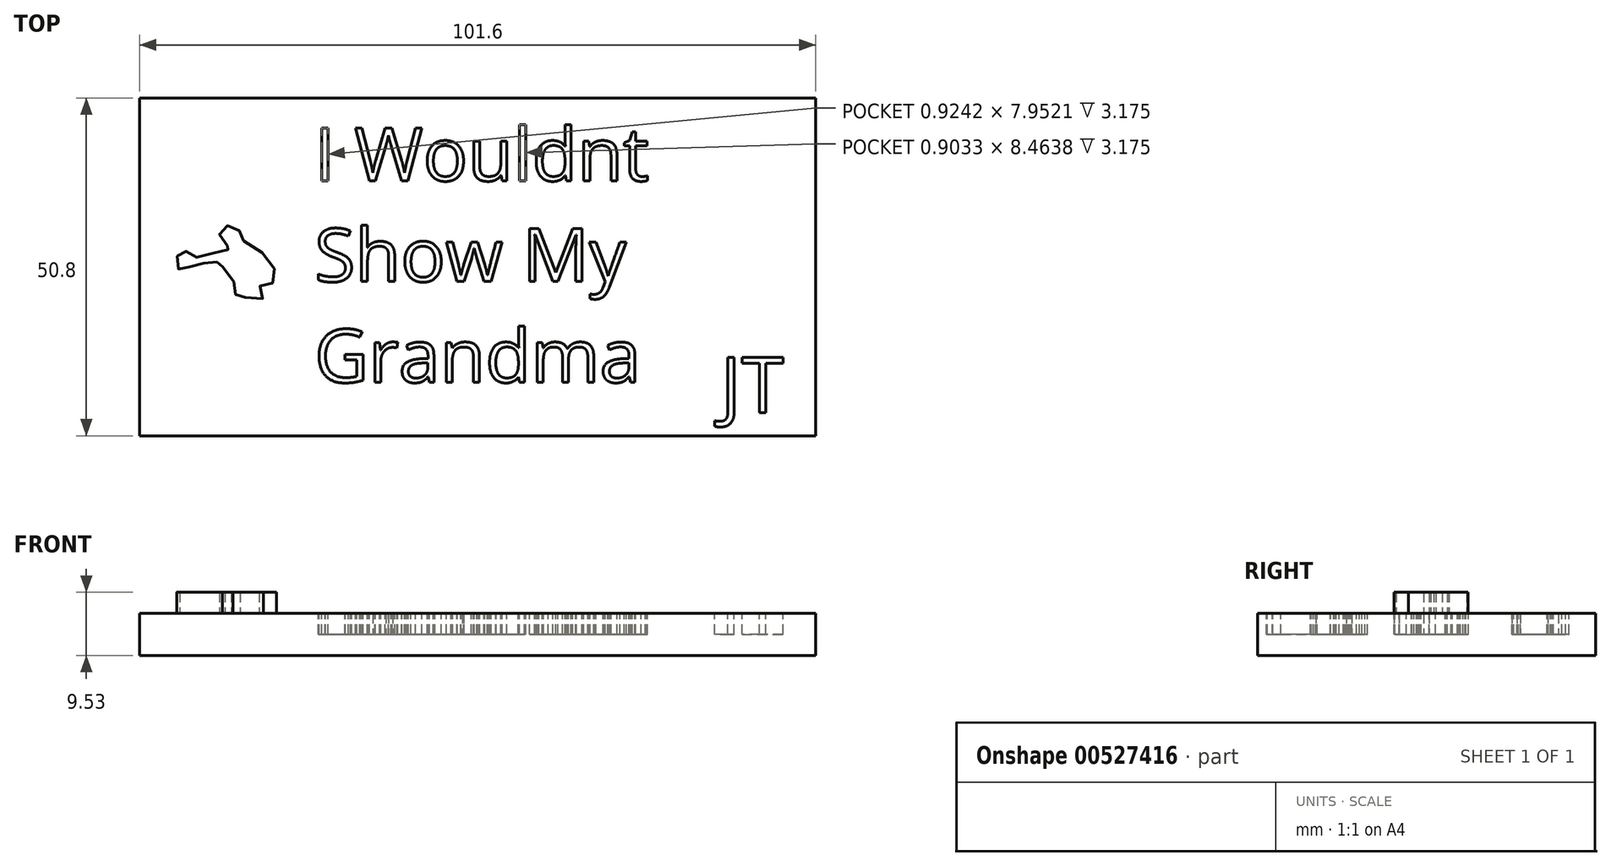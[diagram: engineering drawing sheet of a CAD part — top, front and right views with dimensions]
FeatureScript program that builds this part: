
annotation { "Feature Type Name" : "Feature", "Feature Type Description" : "" }
export const myFeature = defineFeature(function(context is Context, id is Id, definition is map)
    precondition{}
    {
        {
            var Q0;
            Q0=qCreatedBy(makeId("Top.planeOp"),FACE);
            var sketch = newSketch(context, id + "F0", { "sketchPlane" : qUnion([Q0])});
            skLineSegment(sketch, "E0.bottom", {"start": v(-49.76, 12.5) * mm, "end": v(51.84, 12.5) * mm});
            skLineSegment(sketch, "E0.top", {"start": v(-49.76, -38.3) * mm, "end": v(51.84, -38.3) * mm});
            skLineSegment(sketch, "E0.left", {"start": v(-49.76, 12.5) * mm, "end": v(-49.76, -38.3) * mm});
            skLineSegment(sketch, "E0.right", {"start": v(51.84, 12.5) * mm, "end": v(51.84, -38.3) * mm});
            skSolve(sketch);
        }
        {
            var Q0;
            Q0=makeQuery(id+"F0.imprint","IMPRINT",FACE,{"disambiguationData":[TD([[makeQuery(id+"F0.imprint","IMPRINT",EDGE,{"derivedFrom":sQuery(id+"F0.wireOp",EDGE,"E0.bottom")}),-1.0]])]});
            extrude(context, id + "F1", {"entities" : qUnion([Q0]), "depth" : 6.35 * mm, "offsetDistance" : 25.4 * mm});
        }
        {
            var Q0;
            Q0=makeQuery(id+"F1.opExtrude","CAP_FACE",FACE,{"disambiguationData":[OSD([sQuery(id+"F0.wireOp",EDGE,"E0.bottom"),sQuery(id+"F0.wireOp",EDGE,"E0.top"),sQuery(id+"F0.wireOp",EDGE,"E0.left"),sQuery(id+"F0.wireOp",EDGE,"E0.right")])],"isStart":false});
            var sketch = newSketch(context, id + "F2", { "sketchPlane" : qUnion([Q0])});
            skText(sketch, "E1", { "text": "I Wouldnt\nShow My\nGrandma", "fontName": "OpenSans-Regular.ttf"});
            const initialGuessF2  = {"E1": [-0.02347, 6e-05, 1, 0, 0.00802]};
            skSetInitialGuess(sketch, initialGuessF2);
            skSolve(sketch);
        }
        {
            var Q0;
            Q0=makeQuery(id+"F2.imprint","IMPRINT",FACE,{"disambiguationData":[TD([[makeQuery(id+"F2.imprint","IMPRINT",EDGE,{"derivedFrom":sQuery(id+"F2.wireOp",EDGE,"E1.sketch_text.stroke-0")}),-1.0]])]});
            var Q1;
            Q1=makeQuery(id+"F2.imprint","IMPRINT",FACE,{"disambiguationData":[TD([[makeQuery(id+"F2.imprint","IMPRINT",EDGE,{"derivedFrom":sQuery(id+"F2.wireOp",EDGE,"E1.sketch_text.stroke-4")}),-1.0]])]});
            var Q2;
            Q2=makeQuery(id+"F2.imprint","IMPRINT",FACE,{"disambiguationData":[TD([[makeQuery(id+"F2.imprint","IMPRINT",EDGE,{"derivedFrom":sQuery(id+"F2.wireOp",EDGE,"E1.sketch_text.stroke-41")}),-1.0]])]});
            var Q3;
            Q3=makeQuery(id+"F2.imprint","IMPRINT",FACE,{"disambiguationData":[TD([[makeQuery(id+"F2.imprint","IMPRINT",EDGE,{"derivedFrom":sQuery(id+"F2.wireOp",EDGE,"E1.sketch_text.stroke-58")}),-1.0]])]});
            var Q4;
            Q4=makeQuery(id+"F2.imprint","IMPRINT",FACE,{"disambiguationData":[TD([[makeQuery(id+"F2.imprint","IMPRINT",EDGE,{"derivedFrom":sQuery(id+"F2.wireOp",EDGE,"E1.sketch_text.stroke-86")}),-1.0]])]});
            var Q5;
            Q5=makeQuery(id+"F2.imprint","IMPRINT",FACE,{"disambiguationData":[TD([[makeQuery(id+"F2.imprint","IMPRINT",EDGE,{"derivedFrom":sQuery(id+"F2.wireOp",EDGE,"E1.sketch_text.stroke-103")}),-1.0]])]});
            var Q6;
            Q6=makeQuery(id+"F2.imprint","IMPRINT",FACE,{"disambiguationData":[TD([[makeQuery(id+"F2.imprint","IMPRINT",EDGE,{"derivedFrom":sQuery(id+"F2.wireOp",EDGE,"E1.sketch_text.stroke-122")}),-1.0]])]});
            var Q7;
            Q7=makeQuery(id+"F2.imprint","IMPRINT",FACE,{"disambiguationData":[TD([[makeQuery(id+"F2.imprint","IMPRINT",EDGE,{"derivedFrom":sQuery(id+"F2.wireOp",EDGE,"E1.sketch_text.stroke-147")}),-1.0]])]});
            var Q8;
            Q8=makeQuery(id+"F2.imprint","IMPRINT",FACE,{"disambiguationData":[TD([[makeQuery(id+"F2.imprint","IMPRINT",EDGE,{"derivedFrom":sQuery(id+"F2.wireOp",EDGE,"E1.sketch_text.stroke-182")}),-1.0]])]});
            var Q9;
            Q9=makeQuery(id+"F2.imprint","IMPRINT",FACE,{"disambiguationData":[TD([[makeQuery(id+"F2.imprint","IMPRINT",EDGE,{"derivedFrom":sQuery(id+"F2.wireOp",EDGE,"E1.sketch_text.stroke-205")}),-1.0]])]});
            var Q10;
            Q10=makeQuery(id+"F2.imprint","IMPRINT",FACE,{"disambiguationData":[TD([[makeQuery(id+"F2.imprint","IMPRINT",EDGE,{"derivedFrom":sQuery(id+"F2.wireOp",EDGE,"E1.sketch_text.stroke-223")}),-1.0]])]});
            var Q11;
            Q11=makeQuery(id+"F2.imprint","IMPRINT",FACE,{"disambiguationData":[TD([[makeQuery(id+"F2.imprint","IMPRINT",EDGE,{"derivedFrom":sQuery(id+"F2.wireOp",EDGE,"E1.sketch_text.stroke-239")}),-1.0]])]});
            var Q12;
            Q12=makeQuery(id+"F2.imprint","IMPRINT",FACE,{"disambiguationData":[TD([[makeQuery(id+"F2.imprint","IMPRINT",EDGE,{"derivedFrom":sQuery(id+"F2.wireOp",EDGE,"E1.sketch_text.stroke-259")}),-1.0]])]});
            var Q13;
            Q13=makeQuery(id+"F2.imprint","IMPRINT",FACE,{"disambiguationData":[TD([[makeQuery(id+"F2.imprint","IMPRINT",EDGE,{"derivedFrom":sQuery(id+"F2.wireOp",EDGE,"E1.sketch_text.stroke-299")}),-1.0]])]});
            var Q14;
            Q14=makeQuery(id+"F2.imprint","IMPRINT",FACE,{"disambiguationData":[TD([[makeQuery(id+"F2.imprint","IMPRINT",EDGE,{"derivedFrom":sQuery(id+"F2.wireOp",EDGE,"E1.sketch_text.stroke-340")}),-1.0]])]});
            var Q15;
            Q15=makeQuery(id+"F2.imprint","IMPRINT",FACE,{"disambiguationData":[TD([[makeQuery(id+"F2.imprint","IMPRINT",EDGE,{"derivedFrom":sQuery(id+"F2.wireOp",EDGE,"E1.sketch_text.stroke-24")}),-1.0]])]});
            var Q16;
            Q16=makeQuery(id+"F2.imprint","IMPRINT",FACE,{"disambiguationData":[TD([[makeQuery(id+"F2.imprint","IMPRINT",EDGE,{"derivedFrom":sQuery(id+"F2.wireOp",EDGE,"E1.sketch_text.stroke-62")}),-1.0]])]});
            var Q17;
            Q17=makeQuery(id+"F2.imprint","IMPRINT",FACE,{"disambiguationData":[TD([[makeQuery(id+"F2.imprint","IMPRINT",EDGE,{"derivedFrom":sQuery(id+"F2.wireOp",EDGE,"E1.sketch_text.stroke-165")}),-1.0]])]});
            var Q18;
            Q18=makeQuery(id+"F2.imprint","IMPRINT",FACE,{"disambiguationData":[TD([[makeQuery(id+"F2.imprint","IMPRINT",EDGE,{"derivedFrom":sQuery(id+"F2.wireOp",EDGE,"E1.sketch_text.stroke-272")}),-1.0]])]});
            var Q19;
            Q19=makeQuery(id+"F2.imprint","IMPRINT",FACE,{"disambiguationData":[TD([[makeQuery(id+"F2.imprint","IMPRINT",EDGE,{"derivedFrom":sQuery(id+"F2.wireOp",EDGE,"E1.sketch_text.stroke-316")}),-1.0]])]});
            var Q20;
            Q20=makeQuery(id+"F2.imprint","IMPRINT",FACE,{"disambiguationData":[TD([[makeQuery(id+"F2.imprint","IMPRINT",EDGE,{"derivedFrom":sQuery(id+"F2.wireOp",EDGE,"E1.sketch_text.stroke-368")}),-1.0]])]});
            extrude(context, id + "F3", {"entities" : qUnion([Q0, Q1, Q2, Q3, Q4, Q5, Q6, Q7, Q8, Q9, Q10, Q11, Q12, Q13, Q14, Q15, Q16, Q17, Q18, Q19, Q20]), "operationType" : NewBodyOperationType.REMOVE, "oppositeDirection" : true, "depth" : 3.17 * mm, "offsetDistance" : 25.4 * mm});
        }
        {
            var Q0;
            {var subQ0=sQuery(id+"F0.wireOp",EDGE,"E0.left");var subQ1=sQuery(id+"F0.wireOp",EDGE,"E0.bottom");var subQ2=sQuery(id+"F0.wireOp",EDGE,"E0.right");var subQ3=sQuery(id+"F0.wireOp",EDGE,"E0.top");Q0=makeQuery(id+"F3.boolean.opBoolean","SPLIT",FACE,{"disambiguationData":[TD([makeQuery(id+"F1.opExtrude","SWEPT_FACE",FACE,{"disambiguationData":[OSD([subQ1])]})])],"derivedFrom":makeQuery(id+"F1.opExtrude","CAP_FACE",FACE,{"disambiguationData":[OSD([subQ1,subQ3,subQ0,subQ2])],"isStart":false})});}
            var sketch = newSketch(context, id + "F4", { "sketchPlane" : qUnion([Q0])});
            skText(sketch, "E2", { "text": "JT", "fontName": "OpenSans-Regular.ttf"});
            const initialGuessF4  = {"E2": [0.03757, -0.03479, 1, 0, 0.00835]};
            skSetInitialGuess(sketch, initialGuessF4);
            skSolve(sketch);
        }
        {
            var Q0;
            Q0 = qSketchRegion(id + "F4", true);
            extrude(context, id + "F5", {"entities" : qUnion([Q0]), "operationType" : NewBodyOperationType.REMOVE, "oppositeDirection" : true, "depth" : 3.17 * mm, "offsetDistance" : 25.4 * mm});
        }
        {
            var Q0;
            {var subQ0=sQuery(id+"F0.wireOp",EDGE,"E0.left");var subQ1=sQuery(id+"F0.wireOp",EDGE,"E0.bottom");var subQ2=sQuery(id+"F0.wireOp",EDGE,"E0.right");var subQ3=sQuery(id+"F0.wireOp",EDGE,"E0.top");Q0=makeQuery(id+"F3.boolean.opBoolean","SPLIT",FACE,{"disambiguationData":[TD([makeQuery(id+"F1.opExtrude","SWEPT_FACE",FACE,{"disambiguationData":[OSD([subQ1])]})])],"derivedFrom":makeQuery(id+"F1.opExtrude","CAP_FACE",FACE,{"disambiguationData":[OSD([subQ1,subQ3,subQ0,subQ2])],"isStart":false})});}
            var sketch = newSketch(context, id + "F6", { "sketchPlane" : qUnion([Q0])});
            skFitSpline(sketch, "E3", {"points": [v(-38.13, -12.15) * mm, v(-38.49, -12.23) * mm, v(-39, -12.3) * mm, v(-39.8, -12.27) * mm, v(-41.23, -12.5) * mm, v(-41.93, -12.54) * mm, v(-42.46, -13.03) * mm, v(-43, -13.32) * mm, v(-43.56, -13.31) * mm, v(-43.82, -13.27) * mm, v(-44.07, -13) * mm, v(-44.12, -12.22) * mm, v(-44.1, -11.7) * mm, v(-43.99, -11.05) * mm, v(-43.72, -10.96) * mm, v(-43.72, -10.82) * mm, v(-43.35, -10.6) * mm, v(-42.35, -10.55) * mm, v(-41.7, -10.86) * mm, v(-41.49, -11.32) * mm, v(-40.8, -11.46) * mm, v(-39.7, -11.18) * mm, v(-38.57, -10.8) * mm, v(-37.4, -10.75) * mm, v(-36.68, -10.56) * mm, v(-36.4, -10.18) * mm, v(-36.05, -9.86) * mm, v(-36.02, -9.58) * mm, v(-36.37, -9.6) * mm, v(-36.55, -9.76) * mm, v(-36.93, -9.76) * mm, v(-37.4, -9.39) * mm, v(-37.66, -7.36) * mm, v(-36.97, -6.8) * mm, v(-36.86, -6.88) * mm, v(-36.68, -6.77) * mm, v(-36.27, -6.66) * mm, v(-35.4, -6.81) * mm, v(-34.9, -7.2) * mm, v(-34.59, -7.86) * mm, v(-34.55, -8.37) * mm, v(-34.47, -8.48) * mm, v(-34.17, -8.89) * mm, v(-33.73, -9.07) * mm, v(-31.89, -10.3) * mm, v(-30.04, -11.95) * mm, v(-29.62, -12.98) * mm, v(-29.27, -13.58) * mm, v(-29.22, -14.48) * mm, v(-29.88, -15.38) * mm, v(-30.89, -15.65) * mm, v(-31.75, -15.6) * mm, v(-31.5, -16.02) * mm, v(-31.18, -16.96) * mm, v(-31.15, -17.56) * mm, v(-31.31, -17.67) * mm, v(-32.72, -17.75) * mm, v(-33.66, -17.45) * mm, v(-35, -17.53) * mm, v(-35.71, -17.29) * mm, v(-35.24, -16.96) * mm, v(-34.61, -16.46) * mm, v(-35.37, -15.32) * mm, v(-36.32, -14.44) * mm, v(-37.07, -13.3) * mm, v(-37.24, -12.3) * mm, v(-36.94, -11.8) * mm, v(-38.13, -12.15) * mm]});
            skSolve(sketch);
        }
        {
            var Q0;
            Q0 = qSketchRegion(id + "F6", true);
            extrude(context, id + "F7", {"entities" : qUnion([Q0]), "operationType" : NewBodyOperationType.ADD, "depth" : 3.17 * mm, "offsetDistance" : 25.4 * mm});
        }
    });
